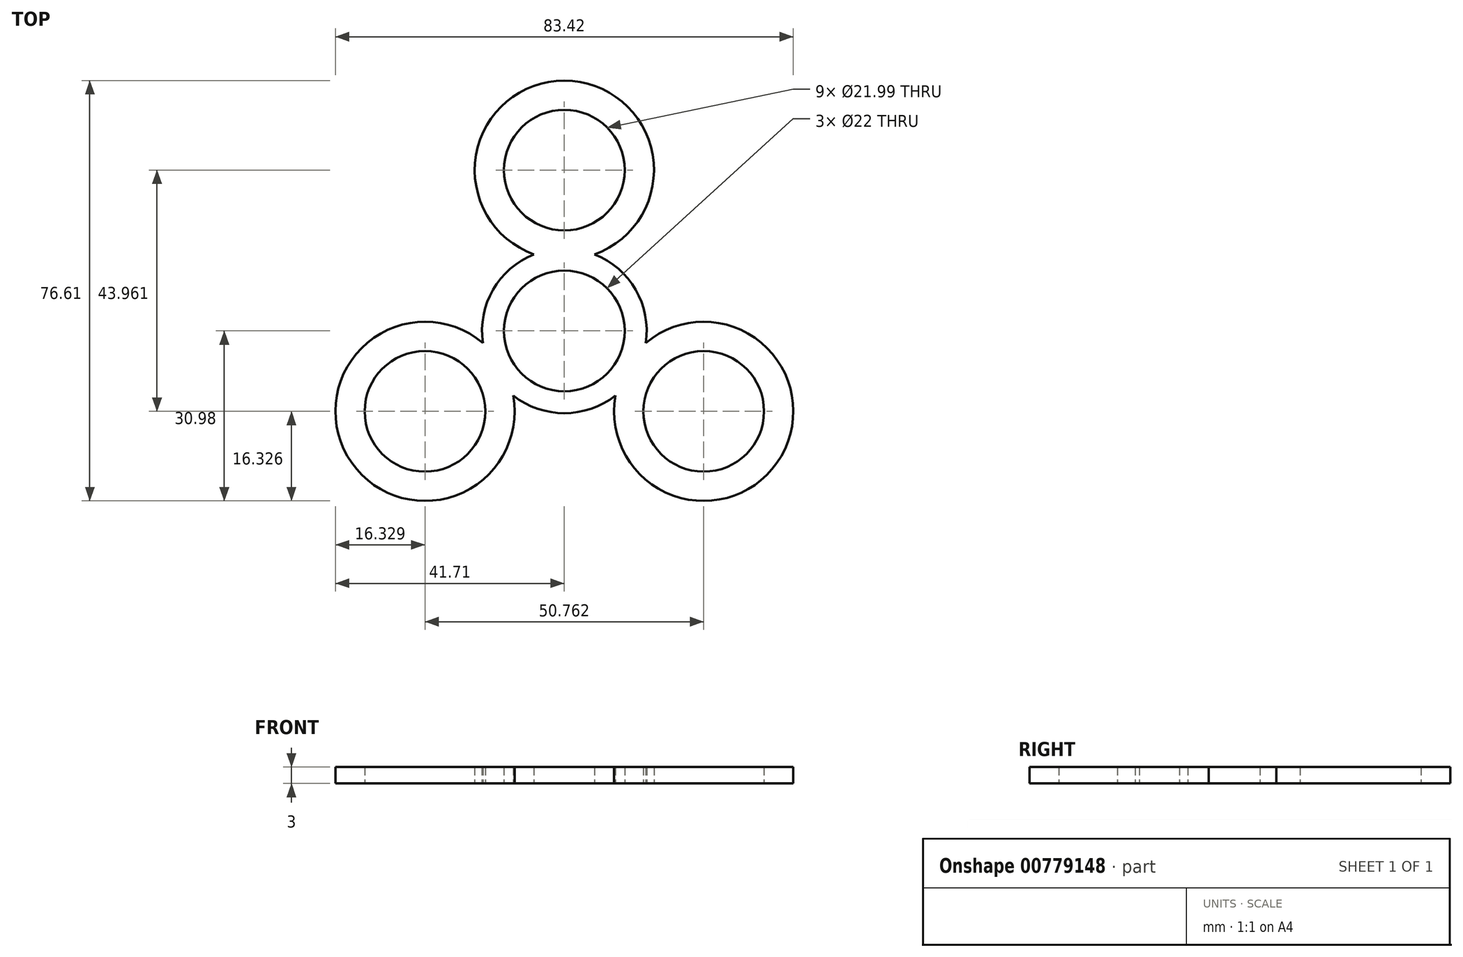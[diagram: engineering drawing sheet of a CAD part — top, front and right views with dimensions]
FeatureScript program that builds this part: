
annotation { "Feature Type Name" : "Feature", "Feature Type Description" : "" }
export const myFeature = defineFeature(function(context is Context, id is Id, definition is map)
    precondition{}
    {
        {
            var Q0;
            Q0=qCreatedBy(makeId("Top.planeOp"),FACE);
            var sketch = newSketch(context, id + "F0", { "sketchPlane" : qUnion([Q0])});
            skArc(sketch, "E0", {"start": v(9.53, 5.5) * mm, "mid": v(0, 11) * mm, "end": v(-9.53, 5.5) * mm});
            skArc(sketch, "E1", {"start": v(13, 7.5) * mm, "mid": v(9.8, 11.35) * mm, "end": v(5.53, 13.94) * mm});
            skArc(sketch, "E2", {"start": v(5.53, 13.94) * mm, "mid": v(0, 45.63) * mm, "end": v(-5.53, 13.94) * mm});
            skCircle(sketch, "E3", {"center": v(0, 29.3) * mm, "radius": 11 * mm});
            skArc(sketch, "E4.trimOffspring", {"start": v(-5.53, 13.94) * mm, "mid": v(-9.8, 11.35) * mm, "end": v(-13, 7.5) * mm});
            skArc(sketch, "E5.1.0", {"start": v(-14.84, -2.18) * mm, "mid": v(-39.52, -22.82) * mm, "end": v(-9.31, -11.76) * mm});
            skCircle(sketch, "E5.1.1", {"center": v(-25.38, -14.65) * mm, "radius": 11 * mm});
            skArc(sketch, "E5.1.2", {"start": v(-9.53, 5.5) * mm, "mid": v(-9.53, -5.5) * mm, "end": v(0, -11) * mm});
            skArc(sketch, "E5.1.3", {"start": v(-9.31, -11.76) * mm, "mid": v(-4.93, -14.17) * mm, "end": v(0, -15) * mm});
            skArc(sketch, "E5.1.4", {"start": v(-13, 7.5) * mm, "mid": v(-14.73, 2.81) * mm, "end": v(-14.84, -2.18) * mm});
            skArc(sketch, "E5.2.0", {"start": v(9.31, -11.76) * mm, "mid": v(39.52, -22.82) * mm, "end": v(14.84, -2.18) * mm});
            skCircle(sketch, "E5.2.1", {"center": v(25.38, -14.65) * mm, "radius": 11 * mm});
            skArc(sketch, "E5.2.2", {"start": v(0, -11) * mm, "mid": v(9.53, -5.5) * mm, "end": v(9.53, 5.5) * mm});
            skArc(sketch, "E5.2.3", {"start": v(14.84, -2.18) * mm, "mid": v(14.73, 2.81) * mm, "end": v(13, 7.5) * mm});
            skArc(sketch, "E5.2.4", {"start": v(0, -15) * mm, "mid": v(4.93, -14.17) * mm, "end": v(9.31, -11.76) * mm});
            skSolve(sketch);
        }
        {
            var Q0;
            Q0 = qSketchRegion(id + "F0", true);
            extrude(context, id + "F1", {"entities" : qUnion([Q0]), "depth" : 3 * mm, "offsetDistance" : 25 * mm});
        }
    });
